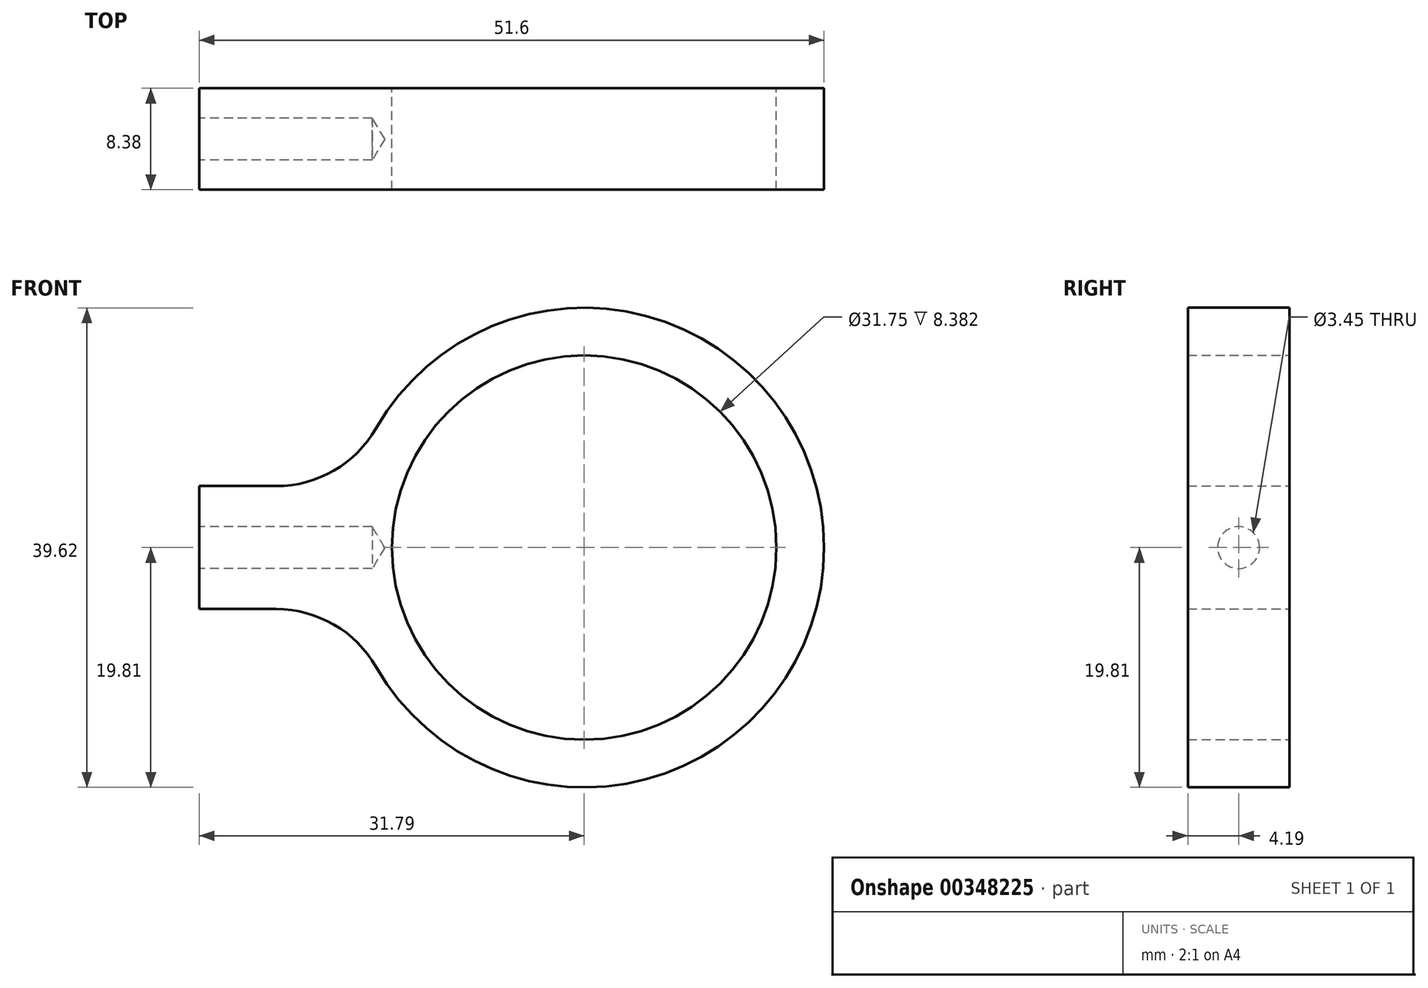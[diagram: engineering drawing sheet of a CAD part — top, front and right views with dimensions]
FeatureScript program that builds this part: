
annotation { "Feature Type Name" : "Feature", "Feature Type Description" : "" }
export const myFeature = defineFeature(function(context is Context, id is Id, definition is map)
    precondition{}
    {
        {
            var Q0;
            Q0=qCreatedBy(makeId("Front.planeOp"),FACE);
            var sketch = newSketch(context, id + "F0", { "sketchPlane" : qUnion([Q0])});
            skCircle(sketch, "E0", {"center": v(0, 0) * mm, "radius": 15.88 * mm});
            skArc(sketch, "E1", {"start": v(-17.18, 9.86) * mm, "mid": v(19.81, 0) * mm, "end": v(-17.18, -9.86) * mm});
            skLineSegment(sketch, "E2", {"start": v(-25.44, -5.08) * mm, "end": v(-31.8, -5.08) * mm});
            skLineSegment(sketch, "E3", {"start": v(-31.8, -5.08) * mm, "end": v(-31.8, 5.08) * mm});
            skLineSegment(sketch, "E4", {"start": v(-31.8, 5.08) * mm, "end": v(-25.44, 5.08) * mm});
            skPoint(sketch, "E5", {"position": v(-31.8, 0) * mm});
            skPoint(sketch, "E6.visualSharp", {"position": v(-19.15, 5.08) * mm});
            skArc(sketch, "E6.filletArc", {"start": v(-25.44, 5.08) * mm, "mid": v(-20.67, 6.36) * mm, "end": v(-17.18, 9.86) * mm});
            skPoint(sketch, "E7.visualSharp", {"position": v(-19.15, -5.08) * mm});
            skArc(sketch, "E7.filletArc", {"start": v(-17.18, -9.86) * mm, "mid": v(-20.67, -6.36) * mm, "end": v(-25.44, -5.08) * mm});
            skSolve(sketch);
        }
        {
            var Q0;
            Q0=qSketchRegion(id+"F0",true);
            extrude(context, id + "F1", {"entities" : qUnion([Q0]), "endBound" : BoundingType.SYMMETRIC, "depth" : 8.38 * mm});
        }
        {
            var Q0;
            Q0=makeQuery(id+"F1.opExtrude","SWEPT_FACE",FACE,{"disambiguationData":[OSD([sQuery(id+"F0.wireOp",EDGE,"E3")])]});
            var sketch = newSketch(context, id + "F2", { "sketchPlane" : qUnion([Q0])});
            skPoint(sketch, "E8", {"position": v(0, 0) * mm});
            skSolve(sketch);
        }
        {
            var Q0;
            Q0=sQuery(id+"F2.wireOp",VERTEX,"E8");
            var Q1;
            Q1=makeQuery(id+"F1.opExtrude","SWEPT_BODY",BODY,{"disambiguationData":[OSD([sQuery(id+"F0.wireOp",EDGE,"E0"),sQuery(id+"F0.wireOp",EDGE,"E1"),sQuery(id+"F0.wireOp",EDGE,"E2"),sQuery(id+"F0.wireOp",EDGE,"E3"),sQuery(id+"F0.wireOp",EDGE,"E4"),sQuery(id+"F0.wireOp",EDGE,"E6.filletArc"),sQuery(id+"F0.wireOp",EDGE,"E7.filletArc")])]});
            hole(context, id + "F3", {"style" : HoleStyle.SIMPLE, "holeDiameter" : 3.45 * mm, "endStyle" : HoleEndStyle.BLIND, "holeDepth" : 14.29 * mm, "locations" : qUnion([Q0]), "scope" : qUnion([Q1])});
        }
    });
